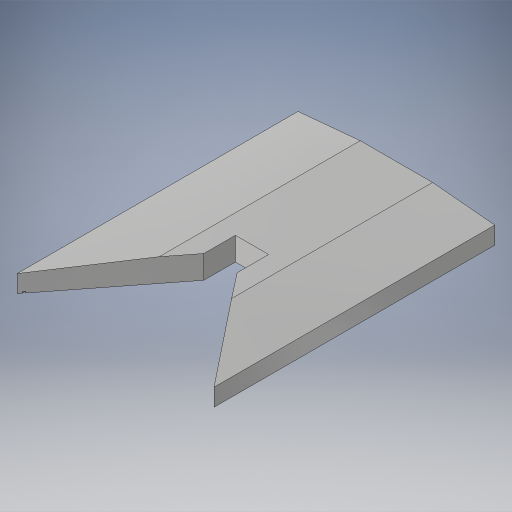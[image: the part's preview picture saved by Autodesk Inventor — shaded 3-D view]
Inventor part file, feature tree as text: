
AUTODESK INVENTOR PART (.ipt)
format: ipt  version: 2023.2 (Build 272271000, 271)  size: 283,648 bytes
history: native  units: in
note: dims shown in document units (in); Inventor stores cm internally (conversion verified against a paired STEP export)
features: extrude x1, sketch x1
ambient origin geometry x8: Origin, YZ Plane, XZ Plane, XY Plane, X Axis, Y Axis, Z Axis, Center Point
bodies: Solid1 (feature_tree)
feature tree (2):
  extrude  "Extrusion1"  Depth=0.375in
  sketch  "Sketch2"  dims[d3=0.375in d4=0.375in d5=0.25in d6=0.25in d7=0.25in d8=0.0in]
